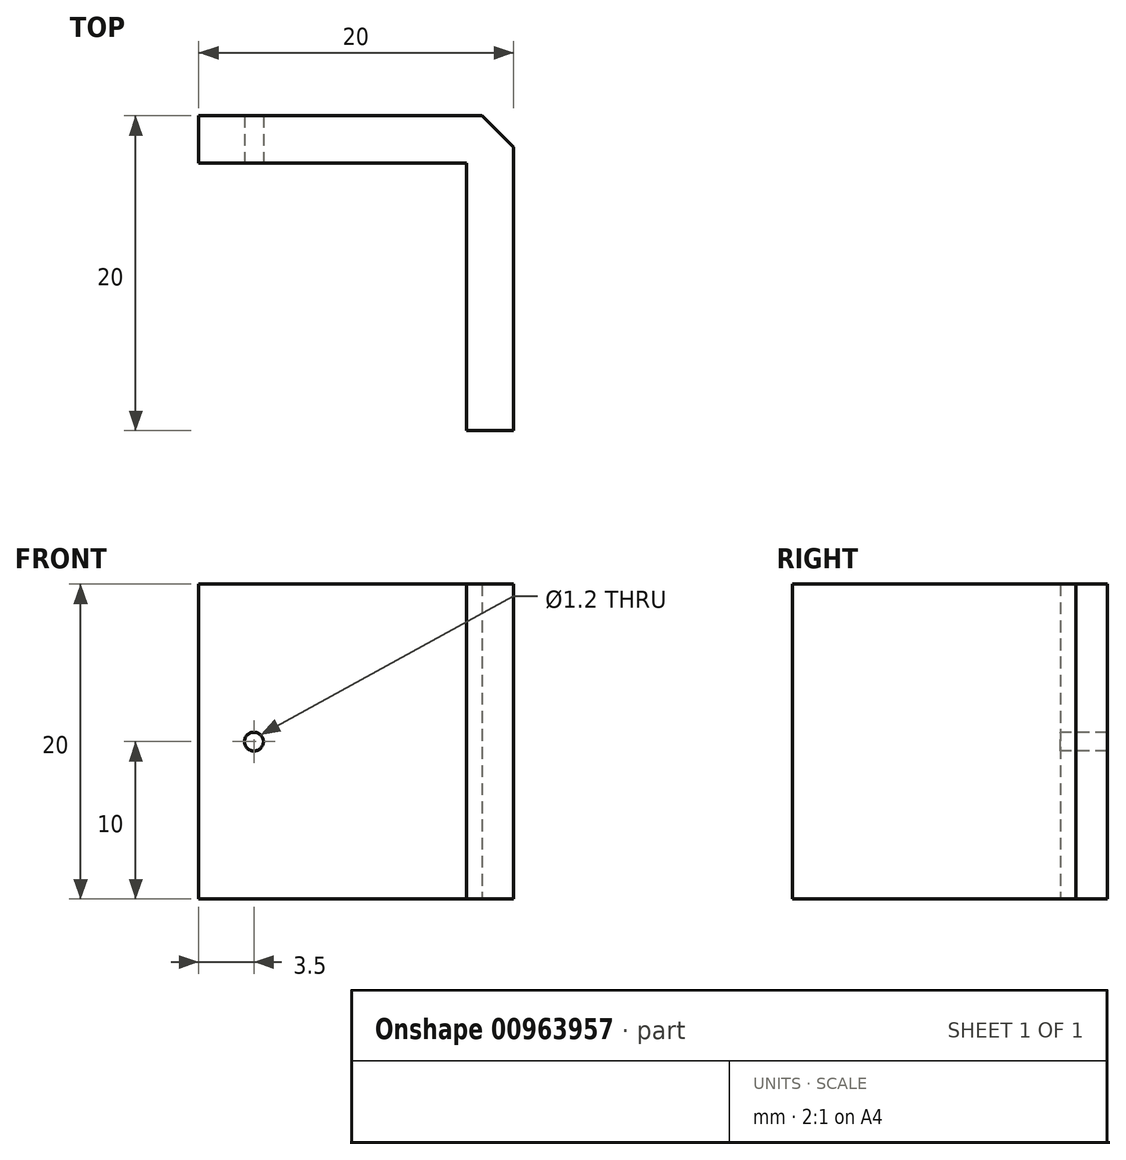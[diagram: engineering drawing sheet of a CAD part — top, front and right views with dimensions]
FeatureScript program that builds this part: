
annotation { "Feature Type Name" : "Feature", "Feature Type Description" : "" }
export const myFeature = defineFeature(function(context is Context, id is Id, definition is map)
    precondition{}
    {
        {
            var Q0;
            Q0=qCreatedBy(makeId("Top.planeOp"),FACE);
            var sketch = newSketch(context, id + "F0", { "sketchPlane" : qUnion([Q0])});
            skLineSegment(sketch, "E0.bottom", {"start": v(-8.5, 1.5) * mm, "end": v(8.5, 1.5) * mm});
            skLineSegment(sketch, "E0.top", {"start": v(-8.5, -1.5) * mm, "end": v(8.5, -1.5) * mm});
            skLineSegment(sketch, "E0.left", {"start": v(-8.5, 1.5) * mm, "end": v(-8.5, -1.5) * mm});
            skPoint(sketch, "E0.middle", {"position": v(0, 0) * mm});
            skLineSegment(sketch, "E1.bottom", {"start": v(8.5, 1.5) * mm, "end": v(11.5, 1.5) * mm});
            skLineSegment(sketch, "E1.top", {"start": v(8.5, -18.5) * mm, "end": v(11.5, -18.5) * mm});
            skLineSegment(sketch, "E1.left", {"start": v(8.5, -1.5) * mm, "end": v(8.5, -18.5) * mm});
            skLineSegment(sketch, "E1.right", {"start": v(11.5, 1.5) * mm, "end": v(11.5, -18.5) * mm});
            skSolve(sketch);
        }
        {
            var Q0;
            Q0 = qSketchRegion(id + "F0", true);
            extrude(context, id + "F1", {"entities" : qUnion([Q0]), "endBound" : BoundingType.SYMMETRIC, "depth" : 20 * mm, "offsetDistance" : 25 * mm});
        }
        {
            var Q0;
            Q0=makeQuery(id+"F1.opExtrude","SWEPT_EDGE",EDGE,{"disambiguationData":[OSD([sQuery(id+"F0.wireOp",EDGE,"E1.bottom"),sQuery(id+"F0.wireOp",EDGE,"E1.right")])]});
            chamfer(context, id + "F2", {"entities" : qUnion([Q0]), "width" : 2 * mm, "tangentPropagation" : true});
        }
        {
            var Q0;
            Q0=makeQuery(id+"F1.opExtrude","SWEPT_FACE",FACE,{"disambiguationData":[OSD([sQuery(id+"F0.wireOp",EDGE,"E0.top")])]});
            var sketch = newSketch(context, id + "F3", { "sketchPlane" : qUnion([Q0])});
            skPoint(sketch, "E2", {"position": v(-5, 0) * mm});
            skSolve(sketch);
        }
        {
            var Q0;
            Q0=sQuery(id+"F3.wireOp",VERTEX,"E2");
            var Q1;
            Q1=makeQuery(id+"F1.opExtrude","SWEPT_BODY",BODY,{"disambiguationData":[OSD([sQuery(id+"F0.wireOp",EDGE,"E0.bottom"),sQuery(id+"F0.wireOp",EDGE,"E0.top"),sQuery(id+"F0.wireOp",EDGE,"E0.left"),sQuery(id+"F0.wireOp",EDGE,"E1.bottom"),sQuery(id+"F0.wireOp",EDGE,"E1.top"),sQuery(id+"F0.wireOp",EDGE,"E1.left"),sQuery(id+"F0.wireOp",EDGE,"E1.right")])]});
            hole(context, id + "F4", {"style" : HoleStyle.SIMPLE, "endStyle" : HoleEndStyle.BLIND, "standardTappedOrClearance" : lookupTablePath({ "fit" : "Normal", "standard" : "ISO", "size" : "M1", "type" : "Clearance" }), "standardBlindInLast" : lookupTablePath({ "fit" : "Normal", "standard" : "ISO", "engagement" : "75%", "pitch" : "0.2 mm", "size" : "M1", "type" : "Clearance & tapped" }), "holeDiameter" : 1.2 * mm, "majorDiameter" : 5 * mm, "holeDepth" : 4 * mm, "isTappedThrough" : true, "tappedDepth" : 28.5 * mm, "tapClearance" : 3, "startFromSketch" : true, "locations" : qUnion([Q0]), "scope" : qUnion([Q1])});
        }
        {
            var Q0;
            Q0=qCreatedBy(makeId("Top.planeOp"),FACE);
            var sketch = newSketch(context, id + "F5", { "sketchPlane" : qUnion([Q0])});
            skLineSegment(sketch, "E3", {"start": v(0, 20.23) * mm, "end": v(0, -21.14) * mm, "construction": true});
            skSolve(sketch);
        }
    });
